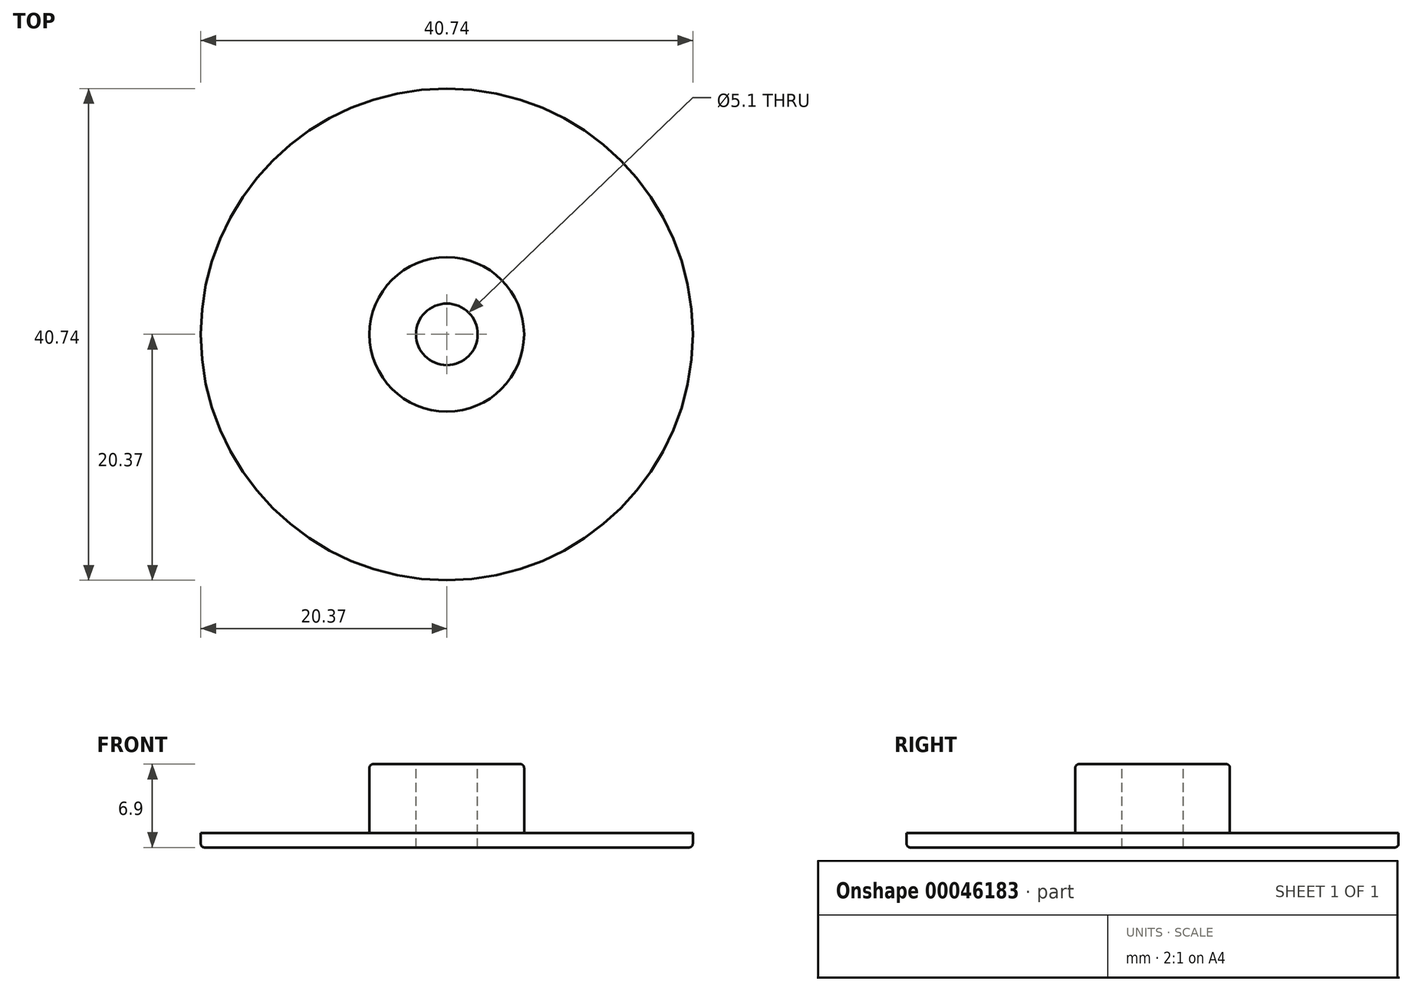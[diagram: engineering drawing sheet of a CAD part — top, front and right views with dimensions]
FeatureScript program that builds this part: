
annotation { "Feature Type Name" : "Feature", "Feature Type Description" : "" }
export const myFeature = defineFeature(function(context is Context, id is Id, definition is map)
    precondition{}
    {
        {
            var Q0;
            Q0=qCreatedBy(makeId("Top.planeOp"),FACE);
            var sketch = newSketch(context, id + "F0", { "sketchPlane" : qUnion([Q0])});
            skCircle(sketch, "E0", {"center": v(0, 0) * mm, "radius": 20.37 * mm});
            skLineSegment(sketch, "E1", {"start": v(0, 0) * mm, "end": v(0, 20.37) * mm, "construction": true});
            skCircle(sketch, "E2.0", {"center": v(0, 0) * mm, "radius": 6.4 * mm});
            skCircle(sketch, "E3", {"center": v(0, 0) * mm, "radius": 2.55 * mm});
            skSolve(sketch);
        }
        {
            var Q0;
            Q0=makeQuery(id+"F0.imprint","IMPRINT",FACE,{"disambiguationData":[TD([[makeQuery(id+"F0.imprint","IMPRINT",EDGE,{"derivedFrom":sQuery(id+"F0.wireOp",EDGE,"E2.0")}),1.0]])]});
            var Q1;
            Q1=makeQuery(id+"F0.imprint","IMPRINT",FACE,{"disambiguationData":[TD([[makeQuery(id+"F0.imprint","IMPRINT",EDGE,{"derivedFrom":sQuery(id+"F0.wireOp",EDGE,"E0")}),1.0]])]});
            var Q2;
            Q2=makeQuery(id+"F0.imprint","IMPRINT",FACE,{"disambiguationData":[TD([[makeQuery(id+"F0.imprint","IMPRINT",EDGE,{"derivedFrom":sQuery(id+"F0.wireOp",EDGE,"099355d9-0bc8-428a-ad83-0e7d7c049963.0")}),1.0]])]});
            extrude(context, id + "F1", {"entities" : qUnion([Q0, Q1, Q2]), "oppositeDirection" : true, "depth" : 1.2 * mm});
        }
        {
            var Q0;
            Q0=makeQuery(id+"F0.imprint","IMPRINT",FACE,{"disambiguationData":[TD([[makeQuery(id+"F0.imprint","IMPRINT",EDGE,{"derivedFrom":sQuery(id+"F0.wireOp",EDGE,"E2.0")}),1.0]])]});
            extrude(context, id + "F2", {"entities" : qUnion([Q0]), "operationType" : NewBodyOperationType.ADD, "depth" : 5.7 * mm});
        }
        {
            var Q0;
            Q0=makeQuery(id+"F1.opExtrude","CAP_EDGE",EDGE,{"disambiguationData":[OSD([sQuery(id+"F0.wireOp",EDGE,"E0")])],"isStart":false});
            var Q1;
            Q1=makeQuery(id+"F2.opExtrude","CAP_EDGE",EDGE,{"disambiguationData":[OSD([sQuery(id+"F0.wireOp",EDGE,"E2.0")])],"isStart":false});
            fillet(context, id + "F3", {"entities" : qUnion([Q0, Q1]), "radius" : .3 * mm, "tangentPropagation" : true, "allowEdgeOverflow" : false});
        }
    });
